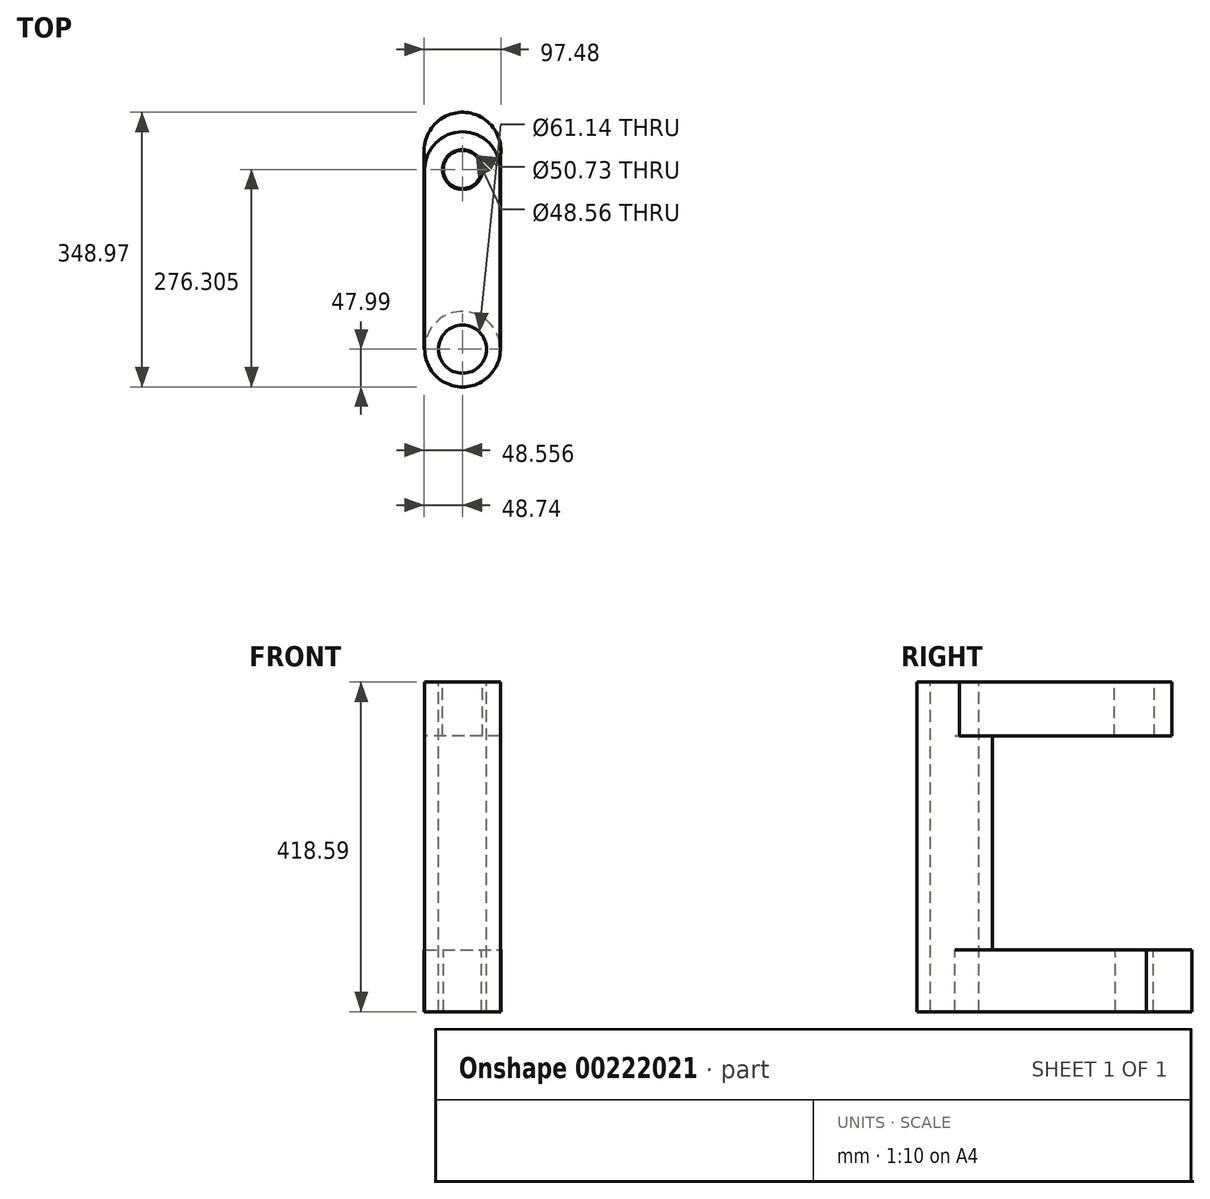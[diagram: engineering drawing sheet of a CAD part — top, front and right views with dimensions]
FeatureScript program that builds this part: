
annotation { "Feature Type Name" : "Feature", "Feature Type Description" : "" }
export const myFeature = defineFeature(function(context is Context, id is Id, definition is map)
    precondition{}
    {
        {
            var Q0;
            Q0=qCreatedBy(makeId("Top.planeOp"),FACE);
            var sketch = newSketch(context, id + "F0", { "sketchPlane" : qUnion([Q0])});
            skCircle(sketch, "E0", {"center": v(0, 0) * mm, "radius": 48 * mm});
            skCircle(sketch, "E1", {"center": v(0, 0) * mm, "radius": 30.57 * mm});
            skSolve(sketch);
        }
        {
            var Q0;
            Q0 = qSketchRegion(id + "F0", true);
            extrude(context, id + "F1", {"entities" : qUnion([Q0]), "oppositeDirection" : true, "depth" : 418.6 * mm});
        }
        {
            var Q0;
            Q0=makeQuery(id+"F1.opExtrude","CAP_FACE",FACE,{"disambiguationData":[OSD([sQuery(id+"F0.wireOp",EDGE,"E0"),sQuery(id+"F0.wireOp",EDGE,"E1")])],"isStart":true});
            var sketch = newSketch(context, id + "F2", { "sketchPlane" : qUnion([Q0])});
            skLineSegment(sketch, "E2.bottom", {"start": v(-48, 0) * mm, "end": v(47.62, 0) * mm});
            skLineSegment(sketch, "E2.top", {"start": v(-48, 228.31) * mm, "end": v(47.62, 228.31) * mm});
            skLineSegment(sketch, "E2.left", {"start": v(-48, 0) * mm, "end": v(-48, 228.31) * mm});
            skLineSegment(sketch, "E2.right", {"start": v(47.62, 0) * mm, "end": v(47.62, 228.31) * mm});
            skCircle(sketch, "E3", {"center": v(-0.18, 228.31) * mm, "radius": 47.8 * mm});
            skCircle(sketch, "E4", {"center": v(-0.18, 228.31) * mm, "radius": 25.37 * mm});
            skSolve(sketch);
        }
        {
            var Q0;
            Q0 = qSketchRegion(id + "F2", true);
            extrude(context, id + "F3", {"entities" : qUnion([Q0]), "operationType" : NewBodyOperationType.ADD, "oppositeDirection" : true, "depth" : 68.58 * mm});
        }
        {
            var Q0;
            Q0=makeQuery(id+"F1.opExtrude","CAP_FACE",FACE,{"disambiguationData":[OSD([sQuery(id+"F0.wireOp",EDGE,"E0"),sQuery(id+"F0.wireOp",EDGE,"E1")])],"isStart":false});
            var sketch = newSketch(context, id + "F4", { "sketchPlane" : qUnion([Q0])});
            skLineSegment(sketch, "E5.bottom", {"start": v(48, 0) * mm, "end": v(-48.74, 0) * mm});
            skLineSegment(sketch, "E5.top", {"start": v(48, -252.23) * mm, "end": v(-48.74, -252.23) * mm});
            skLineSegment(sketch, "E5.left", {"start": v(48, 0) * mm, "end": v(48, -252.23) * mm});
            skLineSegment(sketch, "E5.right", {"start": v(-48.74, 0) * mm, "end": v(-48.74, -252.23) * mm});
            skCircle(sketch, "E6", {"center": v(0, -252.23) * mm, "radius": 48.74 * mm});
            skSolve(sketch);
        }
        {
            var Q0;
            Q0 = qSketchRegion(id + "F4", true);
            extrude(context, id + "F5", {"entities" : qUnion([Q0]), "operationType" : NewBodyOperationType.ADD, "oppositeDirection" : true, "depth" : 78.74 * mm});
        }
        {
            var Q0;
            Q0=makeQuery(id+"F3.boolean.opBoolean","MERGE",FACE,{"derivedFrom":[makeQuery(id+"F1.opExtrude","CAP_FACE",FACE,{"disambiguationData":[OSD([sQuery(id+"F0.wireOp",EDGE,"E0"),sQuery(id+"F0.wireOp",EDGE,"E1")])],"isStart":true}),makeQuery(id+"F3.opExtrude","CAP_FACE",FACE,{"disambiguationData":[OSD([sQuery(id+"F2.wireOp",EDGE,"E2.bottom"),sQuery(id+"F2.wireOp",EDGE,"E2.left"),sQuery(id+"F2.wireOp",EDGE,"E2.right"),sQuery(id+"F2.wireOp",EDGE,"E3"),sQuery(id+"F2.wireOp",EDGE,"E4")])],"isStart":true})]});
            var sketch = newSketch(context, id + "F6", { "sketchPlane" : qUnion([Q0])});
            skCircle(sketch, "E7", {"center": v(0, 0) * mm, "radius": 30.57 * mm});
            skCircle(sketch, "E8", {"center": v(-0.18, 228.31) * mm, "radius": 24.28 * mm});
            skSolve(sketch);
        }
        {
            var Q0;
            Q0 = qSketchRegion(id + "F6", true);
            extrude(context, id + "F7", {"entities" : qUnion([Q0]), "operationType" : NewBodyOperationType.REMOVE, "oppositeDirection" : true, "depth" : 495.3 * mm});
        }
    });
